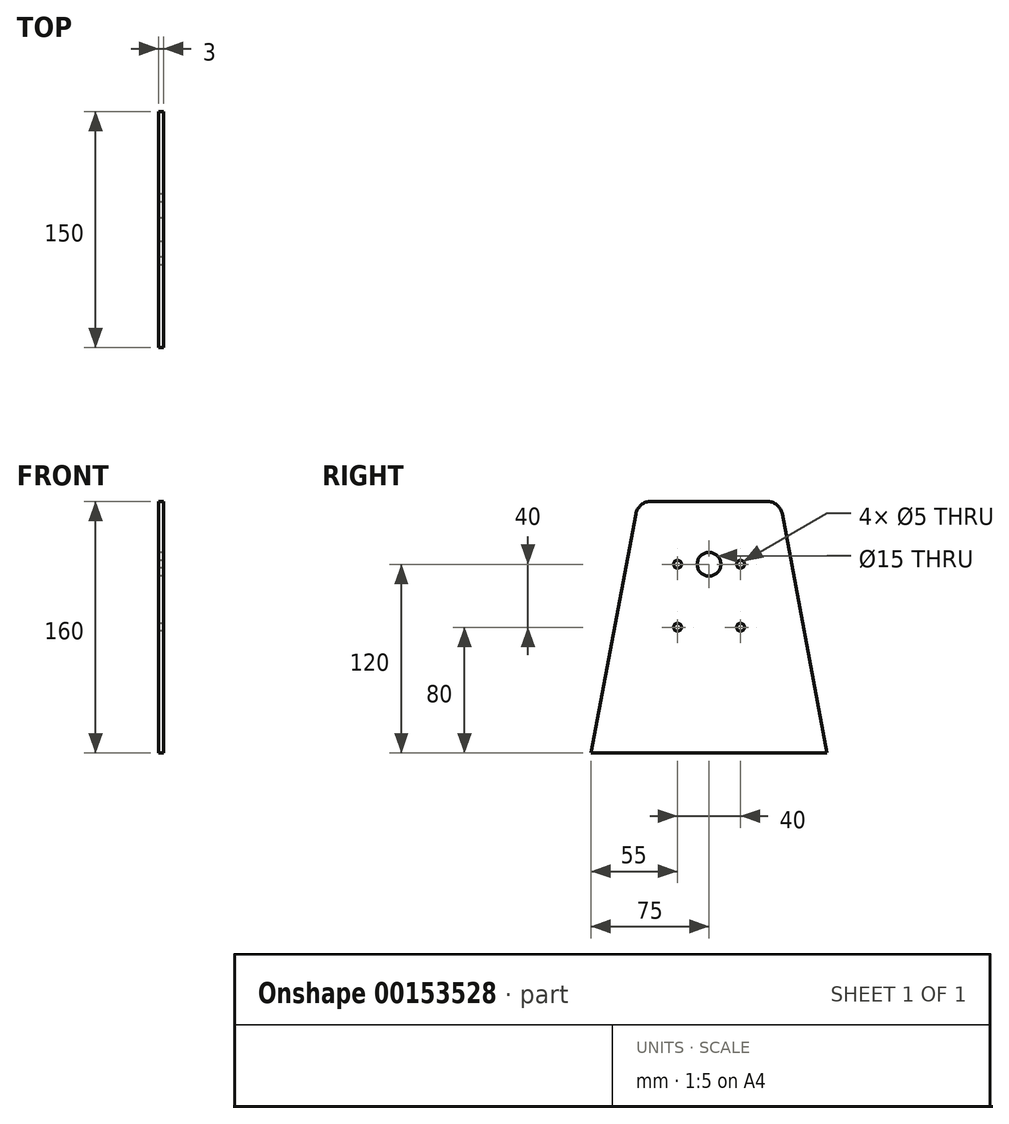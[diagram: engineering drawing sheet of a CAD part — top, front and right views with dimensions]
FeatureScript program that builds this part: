
annotation { "Feature Type Name" : "Feature", "Feature Type Description" : "" }
export const myFeature = defineFeature(function(context is Context, id is Id, definition is map)
    precondition{}
    {
        {
            var Q0;
            Q0=qCreatedBy(makeId("Right.planeOp"),FACE);
            var sketch = newSketch(context, id + "F0", { "sketchPlane" : qUnion([Q0])});
            skLineSegment(sketch, "E0", {"start": v(0, 160) * mm, "end": v(-45, 160) * mm});
            skLineSegment(sketch, "E1", {"start": v(-45, 160) * mm, "end": v(-75, 0) * mm});
            skLineSegment(sketch, "E2", {"start": v(-75, 0) * mm, "end": v(0, 0) * mm});
            skLineSegment(sketch, "E3.MirrorCS", {"start": v(75, 0) * mm, "end": v(0, 0) * mm});
            skLineSegment(sketch, "E4.MirrorCS", {"start": v(45, 160) * mm, "end": v(75, 0) * mm});
            skLineSegment(sketch, "E5.MirrorCS", {"start": v(0, 160) * mm, "end": v(45, 160) * mm});
            skCircle(sketch, "E6", {"center": v(0, 120) * mm, "radius": 7.5 * mm});
            skCircle(sketch, "E7", {"center": v(-20, 120) * mm, "radius": 2.5 * mm});
            skCircle(sketch, "E8", {"center": v(-20, 80) * mm, "radius": 2.5 * mm});
            skCircle(sketch, "E9.MirrorC", {"center": v(20, 80) * mm, "radius": 2.5 * mm});
            skCircle(sketch, "E10.MirrorC", {"center": v(20, 120) * mm, "radius": 2.5 * mm});
            skLineSegment(sketch, "E11", {"start": v(0, 131.22) * mm, "end": v(0, 107.25) * mm});
            skLineSegment(sketch, "E12", {"start": v(12.92, 120) * mm, "end": v(-11.03, 120) * mm});
            skLineSegment(sketch, "E13", {"start": v(20, 124.06) * mm, "end": v(20, 114.5) * mm});
            skLineSegment(sketch, "E14", {"start": v(25.59, 120) * mm, "end": v(15.4, 120) * mm});
            skLineSegment(sketch, "E15", {"start": v(20, 84.12) * mm, "end": v(20, 77.5) * mm});
            skLineSegment(sketch, "E16", {"start": v(24.75, 80) * mm, "end": v(15.46, 80) * mm});
            skLineSegment(sketch, "E17", {"start": v(-20, 85.38) * mm, "end": v(-20, 74.52) * mm});
            skLineSegment(sketch, "E18", {"start": v(-13.38, 80) * mm, "end": v(-26.11, 80) * mm});
            skLineSegment(sketch, "E19", {"start": v(-20, 113.48) * mm, "end": v(-20, 127.39) * mm});
            skLineSegment(sketch, "E20", {"start": v(-14.68, 120) * mm, "end": v(-27.27, 120) * mm});
            skSolve(sketch);
        }
        {
            var Q0;
            Q0=makeQuery(id+"F0.imprint","IMPRINT",FACE,{"disambiguationData":[TD([[makeQuery(id+"F0.imprint","IMPRINT",EDGE,{"derivedFrom":sQuery(id+"F0.wireOp",EDGE,"E0")}),1.0]])]});
            extrude(context, id + "F1", {"entities" : qUnion([Q0]), "depth" : 3 * mm});
        }
        {
            var Q0;
            Q0=makeQuery(id+"F1.opExtrude","SWEPT_EDGE",EDGE,{"disambiguationData":[OSD([sQuery(id+"F0.wireOp",EDGE,"E0"),sQuery(id+"F0.wireOp",EDGE,"E1")])]});
            var Q1;
            Q1=makeQuery(id+"F1.opExtrude","SWEPT_EDGE",EDGE,{"disambiguationData":[OSD([sQuery(id+"F0.wireOp",EDGE,"E4.MirrorCS"),sQuery(id+"F0.wireOp",EDGE,"E5.MirrorCS")])]});
            fillet(context, id + "F2", {"entities" : qUnion([Q0, Q1]), "radius" : 10 * mm, "tangentPropagation" : true, "allowEdgeOverflow" : false});
        }
    });
